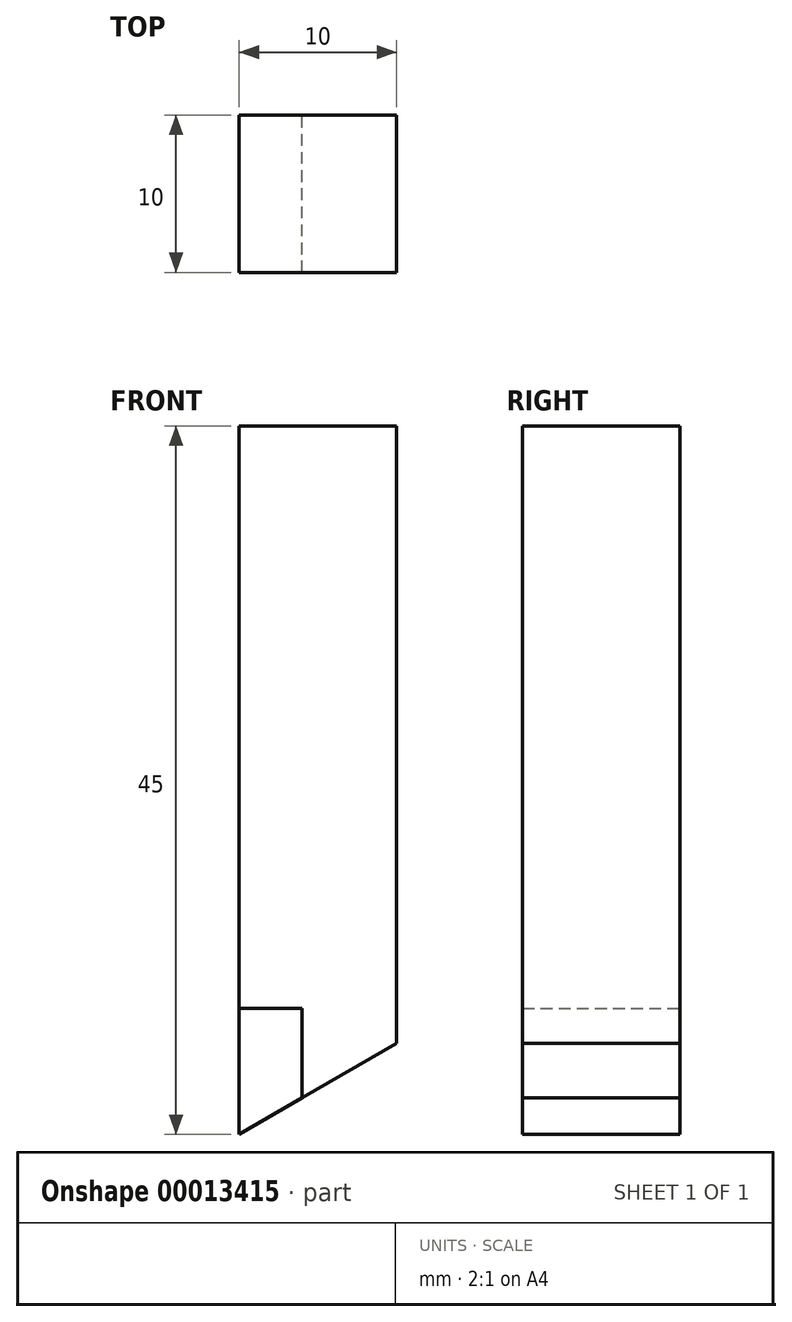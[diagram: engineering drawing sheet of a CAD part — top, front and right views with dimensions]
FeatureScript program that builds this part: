
annotation { "Feature Type Name" : "Feature", "Feature Type Description" : "" }
export const myFeature = defineFeature(function(context is Context, id is Id, definition is map)
    precondition{}
    {
        {
            var Q0;
            Q0=qCreatedBy(makeId("Front.planeOp"),FACE);
            var sketch = newSketch(context, id + "F0", { "sketchPlane" : qUnion([Q0])});
            skLineSegment(sketch, "E0", {"start": v(0, 0) * mm, "end": v(0, 8) * mm});
            skLineSegment(sketch, "E1", {"start": v(0, 8) * mm, "end": v(4, 8) * mm});
            skLineSegment(sketch, "E2", {"start": v(4, 8) * mm, "end": v(4, 2.3) * mm});
            skLineSegment(sketch, "E3", {"start": v(4, 2.3) * mm, "end": v(0, 0) * mm});
            skSolve(sketch);
        }
        {
            var Q0;
            Q0=makeQuery(id+"F0.imprint","IMPRINT",FACE,{"disambiguationData":[TD([[makeQuery(id+"F0.imprint","IMPRINT",EDGE,{"derivedFrom":sQuery(id+"F0.wireOp",EDGE,"E0")}),-1.0]])]});
            extrude(context, id + "F1", {"entities" : qUnion([Q0]), "depth" : 10 * mm});
        }
        {
            var Q0;
            Q0=qCreatedBy(makeId("Front.planeOp"),FACE);
            var sketch = newSketch(context, id + "F2", { "sketchPlane" : qUnion([Q0])});
            skLineSegment(sketch, "E4", {"start": v(0, 0) * mm, "end": v(0, 45) * mm});
            skLineSegment(sketch, "E5", {"start": v(0, 45) * mm, "end": v(10, 45) * mm});
            skLineSegment(sketch, "E6", {"start": v(10, 45) * mm, "end": v(10, 5.77) * mm});
            skLineSegment(sketch, "E7.0", {"start": v(0, 8) * mm, "end": v(4, 8) * mm});
            skLineSegment(sketch, "E8.0", {"start": v(4, 8) * mm, "end": v(4, 2.3) * mm});
            skLineSegment(sketch, "E9", {"start": v(4, 2.3) * mm, "end": v(10, 5.77) * mm});
            skSolve(sketch);
        }
        {
            var Q0;
            {var subQ1=sQuery(id+"F2.wireOp",EDGE,"E5");Q0=makeQuery(id+"F2.imprint","IMPRINT",FACE,{"disambiguationData":[TD([[makeQuery(id+"F2.imprint","IMPRINT",EDGE,{"derivedFrom":subQ1}),-1.0]])]});}
            var Q1;
            Q1=makeQuery(id+"F1.opExtrude","CAP_FACE",FACE,{"disambiguationData":[OSD([sQuery(id+"F0.wireOp",EDGE,"E0"),sQuery(id+"F0.wireOp",EDGE,"E1"),sQuery(id+"F0.wireOp",EDGE,"E2"),sQuery(id+"F0.wireOp",EDGE,"E3")])],"isStart":false});
            extrude(context, id + "F3", {"entities" : qUnion([Q0]), "endBound" : BoundingType.UP_TO_SURFACE, "endBoundEntityFace" : qUnion([Q1]), "depth" : 25 * mm});
        }
    });
